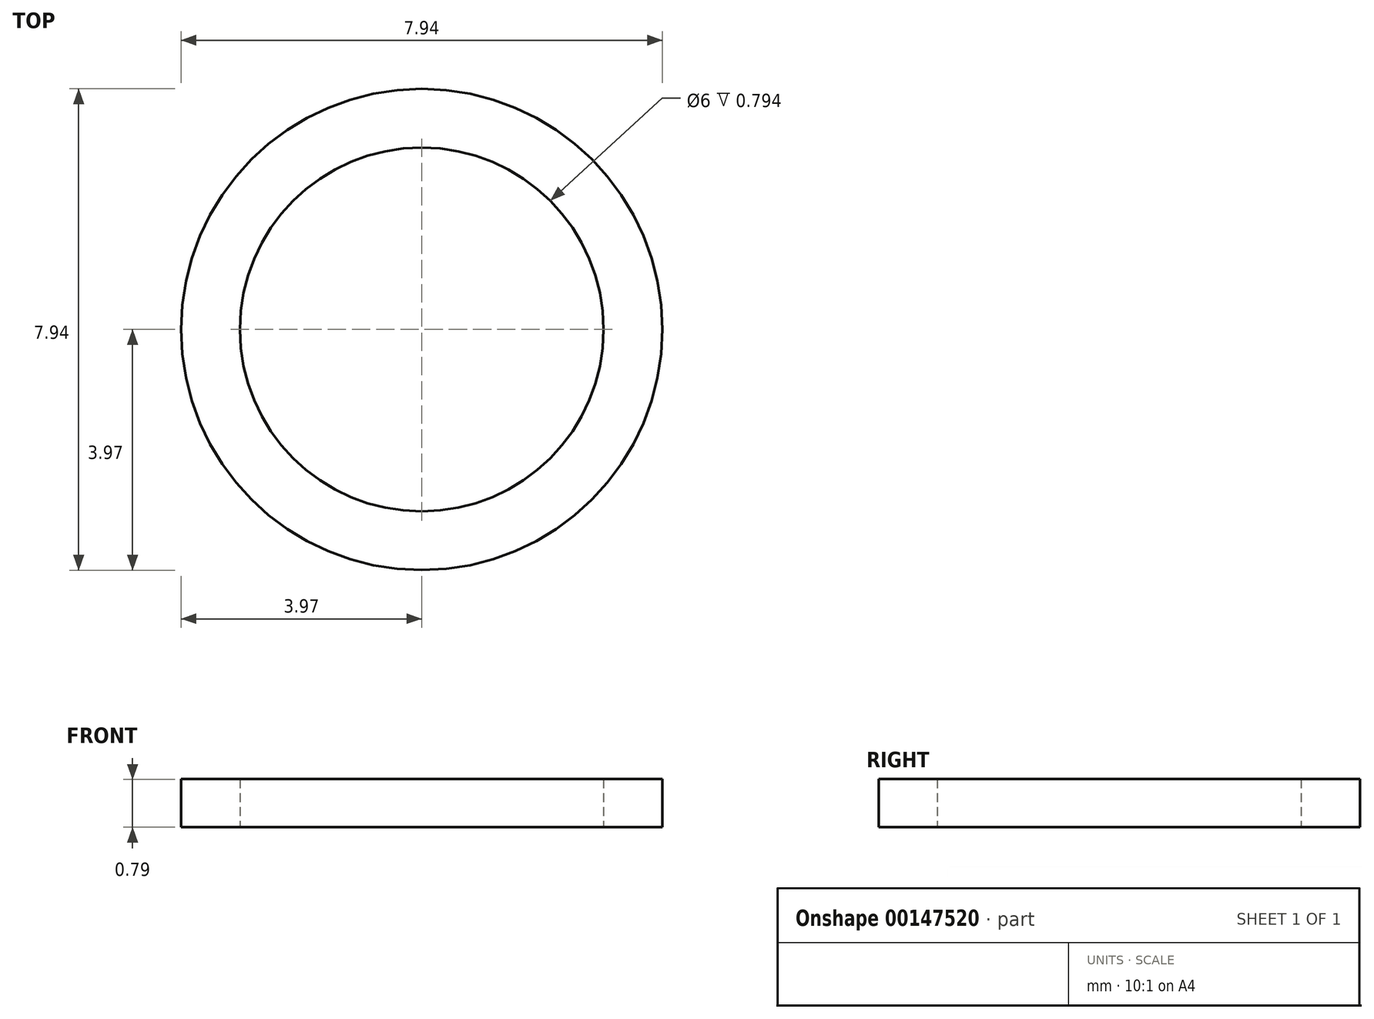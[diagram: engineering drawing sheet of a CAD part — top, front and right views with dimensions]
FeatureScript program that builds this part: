
annotation { "Feature Type Name" : "Feature", "Feature Type Description" : "" }
export const myFeature = defineFeature(function(context is Context, id is Id, definition is map)
    precondition{}
    {
        {
            var Q0;
            Q0=qCreatedBy(makeId("Top.planeOp"),FACE);
            var sketch = newSketch(context, id + "F0", { "sketchPlane" : qUnion([Q0])});
            skCircle(sketch, "E0", {"center": v(0, 0) * mm, "radius": 3 * mm});
            skCircle(sketch, "E1", {"center": v(0, 0) * mm, "radius": 3.97 * mm});
            skSolve(sketch);
        }
        {
            var Q0;
            Q0=qSketchRegion(id+"F0",true);
            extrude(context, id + "F1", {"entities" : qUnion([Q0]), "depth" : 0.8 * mm});
        }
    });
